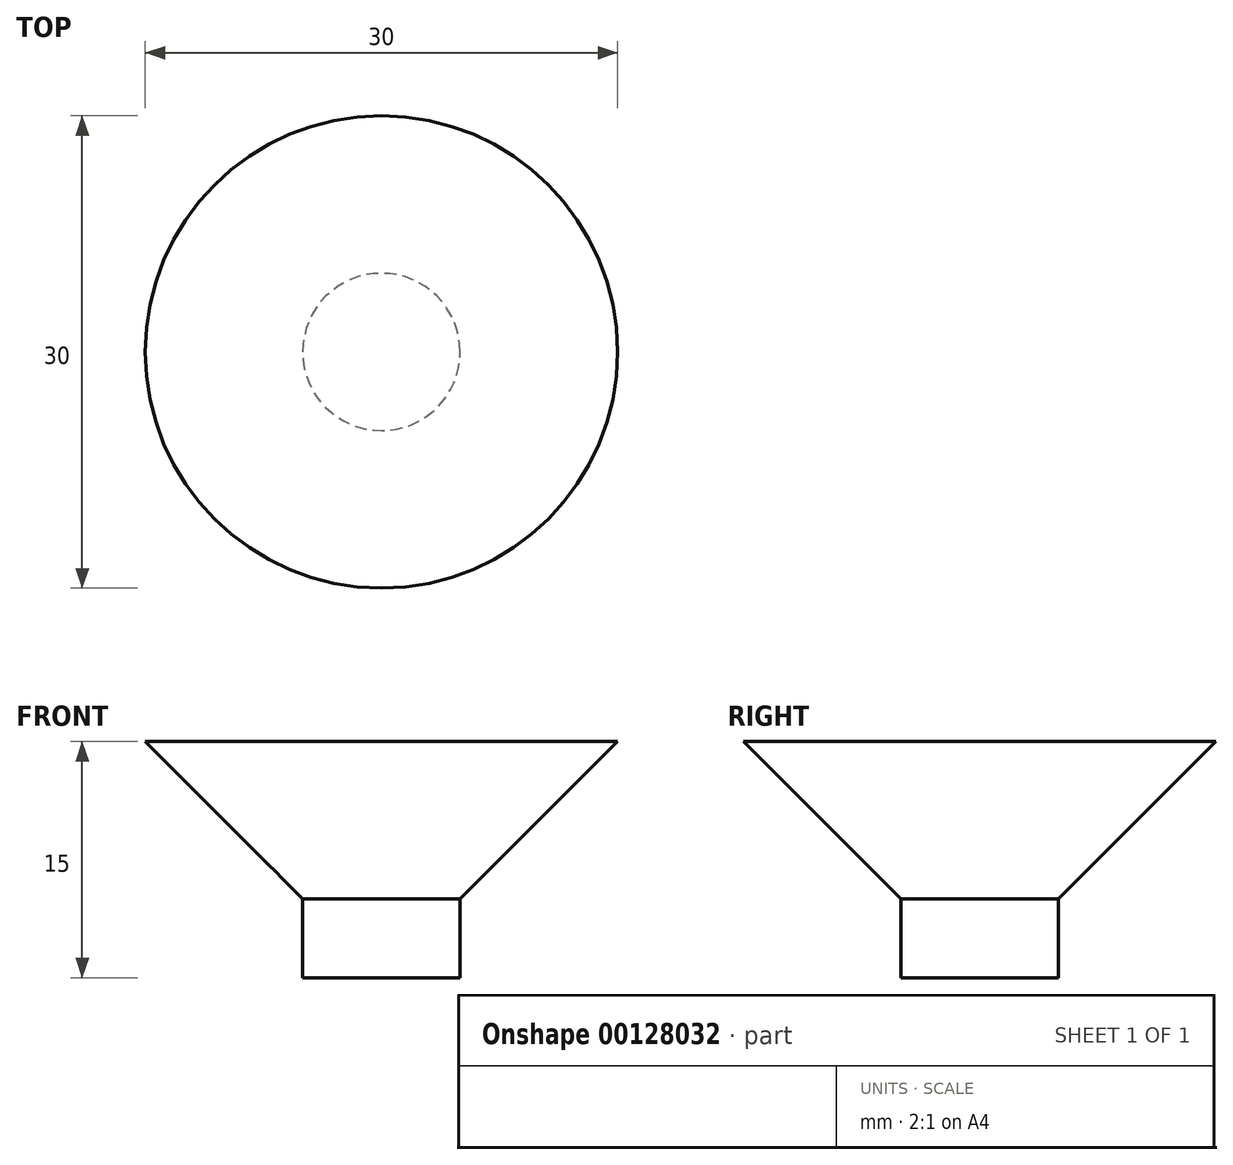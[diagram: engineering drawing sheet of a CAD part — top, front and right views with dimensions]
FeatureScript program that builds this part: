
annotation { "Feature Type Name" : "Feature", "Feature Type Description" : "" }
export const myFeature = defineFeature(function(context is Context, id is Id, definition is map)
    precondition{}
    {
        {
            var Q0;
            Q0=qCreatedBy(makeId("Front.planeOp"),FACE);
            var sketch = newSketch(context, id + "F0", { "sketchPlane" : qUnion([Q0])});
            skLineSegment(sketch, "E0", {"start": v(0, 0) * mm, "end": v(-5, 0) * mm});
            skLineSegment(sketch, "E1", {"start": v(0, 0) * mm, "end": v(0, 15) * mm});
            skLineSegment(sketch, "E2", {"start": v(-15, 15) * mm, "end": v(0, 15) * mm});
            skLineSegment(sketch, "E3", {"start": v(-5, 5) * mm, "end": v(-15, 15) * mm});
            skLineSegment(sketch, "E4", {"start": v(-5, 5) * mm, "end": v(-5, 0) * mm});
            skSolve(sketch);
        }
        {
            var Q0;
            Q0=makeQuery(id+"F0.imprint","IMPRINT",FACE,{"disambiguationData":[TD([[makeQuery(id+"F0.imprint","IMPRINT",EDGE,{"derivedFrom":sQuery(id+"F0.wireOp",EDGE,"E0")}),-1.0]])]});
            var Q1;
            Q1=sQuery(id+"F0.wireOp",EDGE,"E1");
            revolve(context, id + "F1", {"entities" : qUnion([Q0]), "axis" : qUnion([Q1]), "revolveType" : RevolveType.FULL});
        }
    });
